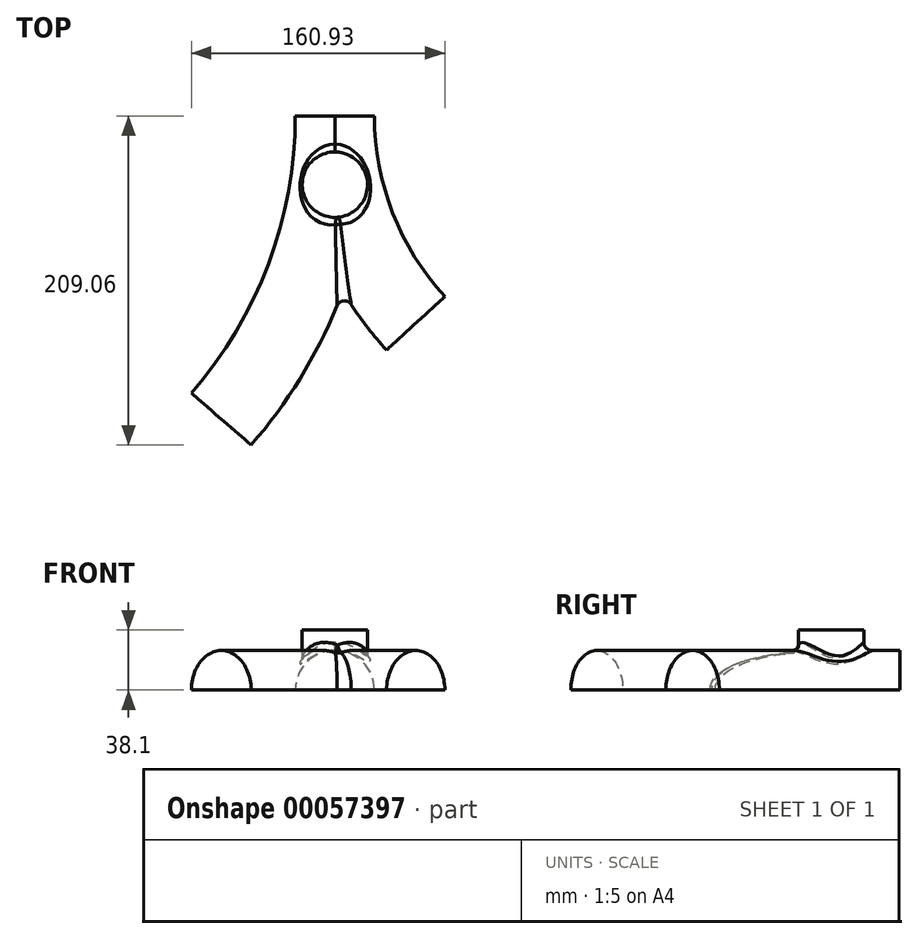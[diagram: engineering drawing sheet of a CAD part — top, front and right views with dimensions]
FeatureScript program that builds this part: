
annotation { "Feature Type Name" : "Feature", "Feature Type Description" : "" }
export const myFeature = defineFeature(function(context is Context, id is Id, definition is map)
    precondition{}
    {
        {
            var Q0;
            Q0=qCreatedBy(makeId("Top.planeOp"),FACE);
            var sketch = newSketch(context, id + "F0", { "sketchPlane" : qUnion([Q0])});
            skLineSegment(sketch, "E0", {"start": v(0, 0) * mm, "end": v(0, -43.68) * mm});
            skCircle(sketch, "E1", {"center": v(0, -43.68) * mm, "radius": 20.77 * mm});
            skSolve(sketch);
        }
        {
            var Q0;
            {var subQ0=sQuery(id+"F0.wireOp",EDGE,"E1");Q0=makeQuery(id+"F0.imprint","IMPRINT",FACE,{"disambiguationData":[TD([[makeQuery(id+"F0.imprint","IMPRINT",EDGE,{"derivedFrom":subQ0}),1.0]])]});}
            extrude(context, id + "F1", {"entities" : qUnion([Q0]), "depth" : 38.1 * mm});
        }
        {
            var Q0;
            Q0=qCreatedBy(makeId("Top.planeOp"),FACE);
            var sketch = newSketch(context, id + "F2", { "sketchPlane" : qUnion([Q0])});
            skArc(sketch, "E2", {"start": v(0, 0) * mm, "mid": v(13.3, -70.7) * mm, "end": v(51.35, -131.73) * mm});
            skArc(sketch, "E3", {"start": v(-72.14, -192.55) * mm, "mid": v(-18.63, -102.8) * mm, "end": v(0, 0) * mm});
            skLineSegment(sketch, "E4", {"start": v(0, 0) * mm, "end": v(0, -167.15) * mm});
            skSolve(sketch);
        }
        {
            var Q0;
            Q0=qCreatedBy(makeId("Front.planeOp"),FACE);
            var sketch = newSketch(context, id + "F3", { "sketchPlane" : qUnion([Q0])});
            skLineSegment(sketch, "E5", {"start": v(25.13, 0) * mm, "end": v(-25.13, 0) * mm});
            skArc(sketch, "E6", {"start": v(25.13, 0) * mm, "mid": v(0, 25.13) * mm, "end": v(-25.13, 0) * mm});
            skSolve(sketch);
        }
        {
            var Q0;
            Q0=makeQuery(id+"F3.imprint","IMPRINT",FACE,{"disambiguationData":[TD([[makeQuery(id+"F3.imprint","IMPRINT",EDGE,{"derivedFrom":sQuery(id+"F3.wireOp",EDGE,"E5")}),-1.0]])]});
            var Q1;
            Q1=sQuery(id+"F2.wireOp",EDGE,"E3");
            sweep(context, id + "F4", {"operationType" : NewBodyOperationType.ADD, "profiles" : qUnion([Q0]), "path" : qUnion([Q1])});
        }
        {
            var Q0;
            Q0=makeQuery(id+"F3.imprint","IMPRINT",FACE,{"disambiguationData":[TD([[makeQuery(id+"F3.imprint","IMPRINT",EDGE,{"derivedFrom":sQuery(id+"F3.wireOp",EDGE,"E5")}),-1.0]])]});
            var Q1;
            Q1=sQuery(id+"F2.wireOp",EDGE,"E2");
            sweep(context, id + "F5", {"operationType" : NewBodyOperationType.ADD, "profiles" : qUnion([Q0]), "path" : qUnion([Q1])});
        }
        {
            var Q0;
            Q0=makeQuery(id+"F5.boolean.opBoolean","INTERSECT",EDGE,{"derivedFrom":[makeQuery(id+"F1.opExtrude","SWEPT_FACE",FACE,{"disambiguationData":[OSD([sQuery(id+"F0.wireOp",EDGE,"E1")])]}),makeQuery(id+"F5.opSweep","SWEPT_FACE",FACE,{"disambiguationData":[OSD([sQuery(id+"F2.wireOp",EDGE,"E2"),sQuery(id+"F3.wireOp",EDGE,"E6")])]})]});
            var Q1;
            Q1=makeQuery(id+"F4.boolean.opBoolean","INTERSECT",EDGE,{"derivedFrom":[makeQuery(id+"F1.opExtrude","SWEPT_FACE",FACE,{"disambiguationData":[OSD([sQuery(id+"F0.wireOp",EDGE,"E1")])]}),makeQuery(id+"F4.opSweep","SWEPT_FACE",FACE,{"disambiguationData":[OSD([sQuery(id+"F2.wireOp",EDGE,"E3"),sQuery(id+"F3.wireOp",EDGE,"E6")])]})]});
            var Q2;
            {var subQ0=sQuery(id+"F3.wireOp",EDGE,"E6");Q2=makeQuery(id+"F5.boolean.opBoolean","INTERSECT",EDGE,{"disambiguationData":[OD(1.0)],"derivedFrom":[makeQuery(id+"F4.opSweep","SWEPT_FACE",FACE,{"disambiguationData":[OSD([sQuery(id+"F2.wireOp",EDGE,"E3"),subQ0])]}),makeQuery(id+"F5.opSweep","SWEPT_FACE",FACE,{"disambiguationData":[OSD([sQuery(id+"F2.wireOp",EDGE,"E2"),subQ0])]})]});}
            fillet(context, id + "F6", {"entities" : qUnion([Q0, Q1, Q2]), "radius" : 5.08 * mm, "tangentPropagation" : true, "allowEdgeOverflow" : false});
        }
    });
